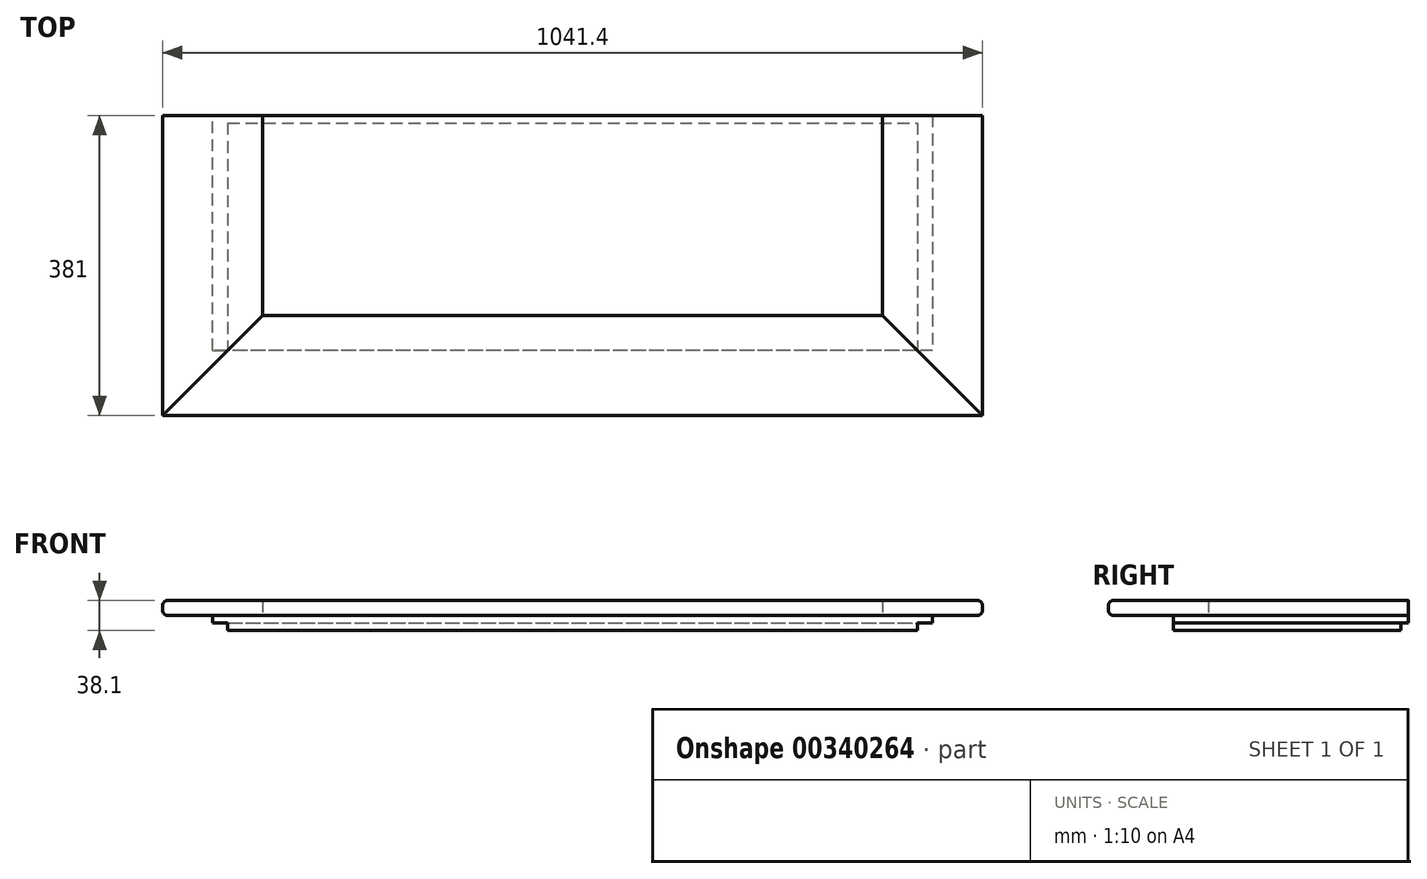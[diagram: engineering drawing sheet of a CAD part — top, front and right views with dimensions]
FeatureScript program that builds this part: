
annotation { "Feature Type Name" : "Feature", "Feature Type Description" : "" }
export const myFeature = defineFeature(function(context is Context, id is Id, definition is map)
    precondition{}
    {
        {
            var Q0;
            Q0=qCreatedBy(makeId("Top.planeOp"),FACE);
            var sketch = newSketch(context, id + "F0", { "sketchPlane" : qUnion([Q0])});
            skLineSegment(sketch, "E0.bottom", {"start": v(457.2, -149.22) * mm, "end": v(-457.2, -149.23) * mm});
            skLineSegment(sketch, "E0.top", {"start": v(457.2, 149.23) * mm, "end": v(-457.2, 149.22) * mm});
            skLineSegment(sketch, "E0.left", {"start": v(457.2, -149.22) * mm, "end": v(457.2, 149.23) * mm});
            skLineSegment(sketch, "E0.right", {"start": v(-457.2, -149.23) * mm, "end": v(-457.2, 149.22) * mm});
            skPoint(sketch, "E0.middle", {"position": v(0, 0) * mm});
            skSolve(sketch);
        }
        {
            var Q0;
            Q0 = qSketchRegion(id + "F0", true);
            extrude(context, id + "F1", {"entities" : qUnion([Q0]), "depth" : 19.05 * mm});
        }
        {
            var Q0;
            Q0=makeQuery(id+"F1.opExtrude","SWEPT_FACE",FACE,{"disambiguationData":[OSD([sQuery(id+"F0.wireOp",EDGE,"E0.left")])]});
            var sketch = newSketch(context, id + "F2", { "sketchPlane" : qUnion([Q0])});
            skLineSegment(sketch, "E1.bottom", {"start": v(149.23, 9.53) * mm, "end": v(139.7, 9.53) * mm});
            skLineSegment(sketch, "E1.top", {"start": v(149.23, 0) * mm, "end": v(139.7, 0) * mm});
            skLineSegment(sketch, "E1.left", {"start": v(149.23, 9.53) * mm, "end": v(149.23, 0) * mm});
            skLineSegment(sketch, "E1.right", {"start": v(139.7, 9.53) * mm, "end": v(139.7, 0) * mm});
            skSolve(sketch);
        }
        {
            var Q0;
            Q0 = qSketchRegion(id + "F2", true);
            extrude(context, id + "F3", {"entities" : qUnion([Q0]), "operationType" : NewBodyOperationType.REMOVE, "endBound" : BoundingType.THROUGH_ALL, "oppositeDirection" : true, "depth" : 25.4 * mm});
        }
        {
            var Q0;
            Q0=makeQuery(id+"F1.opExtrude","SWEPT_FACE",FACE,{"disambiguationData":[OSD([sQuery(id+"F0.wireOp",EDGE,"E0.bottom")])]});
            var sketch = newSketch(context, id + "F4", { "sketchPlane" : qUnion([Q0])});
            skLineSegment(sketch, "E2.bottom", {"start": v(-457.2, 9.53) * mm, "end": v(-438.15, 9.53) * mm});
            skLineSegment(sketch, "E2.top", {"start": v(-457.2, 0) * mm, "end": v(-438.15, 0) * mm});
            skLineSegment(sketch, "E2.left", {"start": v(-457.2, 9.53) * mm, "end": v(-457.2, 0) * mm});
            skLineSegment(sketch, "E2.right", {"start": v(-438.15, 9.53) * mm, "end": v(-438.15, 0) * mm});
            skLineSegment(sketch, "E3", {"start": v(0, 19.05) * mm, "end": v(0, 0) * mm, "construction": true});
            skLineSegment(sketch, "E4.MirrorCS", {"start": v(438.15, 9.52) * mm, "end": v(438.15, 0) * mm});
            skLineSegment(sketch, "E5.MirrorCS", {"start": v(457.2, 9.52) * mm, "end": v(457.2, 0) * mm});
            skLineSegment(sketch, "E6.MirrorCS", {"start": v(457.2, 0) * mm, "end": v(438.15, 0) * mm});
            skLineSegment(sketch, "E7.MirrorCS", {"start": v(457.2, 9.53) * mm, "end": v(438.15, 9.53) * mm});
            skSolve(sketch);
        }
        {
            var Q0;
            Q0 = qSketchRegion(id + "F4", true);
            extrude(context, id + "F5", {"entities" : qUnion([Q0]), "operationType" : NewBodyOperationType.REMOVE, "endBound" : BoundingType.THROUGH_ALL, "oppositeDirection" : true, "depth" : 25.4 * mm});
        }
        {
            var Q0;
            Q0=makeQuery(id+"F1.opExtrude","CAP_FACE",FACE,{"disambiguationData":[OSD([sQuery(id+"F0.wireOp",EDGE,"E0.bottom"),sQuery(id+"F0.wireOp",EDGE,"E0.top"),sQuery(id+"F0.wireOp",EDGE,"E0.left"),sQuery(id+"F0.wireOp",EDGE,"E0.right")])],"isStart":false});
            var sketch = newSketch(context, id + "F6", { "sketchPlane" : qUnion([Q0])});
            skLineSegment(sketch, "E8.bottom", {"start": v(-393.7, -104.78) * mm, "end": v(393.7, -104.77) * mm});
            skLineSegment(sketch, "E8.top", {"start": v(-520.7, -231.78) * mm, "end": v(520.7, -231.77) * mm});
            skLineSegment(sketch, "E9", {"start": v(-520.7, -231.78) * mm, "end": v(-393.7, -104.78) * mm});
            skLineSegment(sketch, "E10", {"start": v(520.7, -231.77) * mm, "end": v(393.7, -104.77) * mm});
            skSolve(sketch);
        }
        {
            var Q0;
            Q0 = qSketchRegion(id + "F6", true);
            extrude(context, id + "F7", {"entities" : qUnion([Q0]), "depth" : 19.05 * mm});
        }
        {
            var Q0;
            Q0=makeQuery(id+"F1.opExtrude","CAP_FACE",FACE,{"disambiguationData":[OSD([sQuery(id+"F0.wireOp",EDGE,"E0.bottom"),sQuery(id+"F0.wireOp",EDGE,"E0.top"),sQuery(id+"F0.wireOp",EDGE,"E0.left"),sQuery(id+"F0.wireOp",EDGE,"E0.right")])],"isStart":false});
            var sketch = newSketch(context, id + "F8", { "sketchPlane" : qUnion([Q0])});
            skLineSegment(sketch, "E11.bottom", {"start": v(-520.7, 149.22) * mm, "end": v(-393.7, 149.22) * mm});
            skLineSegment(sketch, "E11.left", {"start": v(-520.7, 149.22) * mm, "end": v(-520.7, -231.78) * mm});
            skLineSegment(sketch, "E11.right", {"start": v(-393.7, 149.22) * mm, "end": v(-393.7, -104.77) * mm});
            skLineSegment(sketch, "E12", {"start": v(-520.7, -231.78) * mm, "end": v(-393.7, -104.77) * mm});
            skSolve(sketch);
        }
        {
            var Q0;
            Q0 = qSketchRegion(id + "F8", true);
            extrude(context, id + "F9", {"entities" : qUnion([Q0]), "depth" : 19.05 * mm});
        }
        {
            var Q0;
            Q0=makeQuery(id+"F1.opExtrude","CAP_FACE",FACE,{"disambiguationData":[OSD([sQuery(id+"F0.wireOp",EDGE,"E0.bottom"),sQuery(id+"F0.wireOp",EDGE,"E0.top"),sQuery(id+"F0.wireOp",EDGE,"E0.left"),sQuery(id+"F0.wireOp",EDGE,"E0.right")])],"isStart":false});
            var sketch = newSketch(context, id + "F10", { "sketchPlane" : qUnion([Q0])});
            skLineSegment(sketch, "E13.bottom", {"start": v(393.7, 149.23) * mm, "end": v(520.7, 149.23) * mm});
            skLineSegment(sketch, "E13.left", {"start": v(393.7, 149.23) * mm, "end": v(393.7, -104.78) * mm});
            skLineSegment(sketch, "E13.right", {"start": v(520.7, 149.23) * mm, "end": v(520.7, -231.77) * mm});
            skLineSegment(sketch, "E14", {"start": v(520.7, -231.77) * mm, "end": v(393.7, -104.77) * mm});
            skSolve(sketch);
        }
        {
            var Q0;
            Q0 = qSketchRegion(id + "F10", true);
            extrude(context, id + "F11", {"entities" : qUnion([Q0]), "depth" : 19.05 * mm});
        }
        {
            var Q0;
            Q0=makeQuery(id+"F7.opExtrude","CAP_EDGE",EDGE,{"disambiguationData":[OSD([sQuery(id+"F6.wireOp",EDGE,"E8.top")])],"isStart":false});
            var Q1;
            Q1=makeQuery(id+"F7.opExtrude","CAP_EDGE",EDGE,{"disambiguationData":[OSD([sQuery(id+"F6.wireOp",EDGE,"E8.top")])],"isStart":true});
            var Q2;
            Q2=makeQuery(id+"F11.opExtrude","CAP_EDGE",EDGE,{"disambiguationData":[OSD([sQuery(id+"F10.wireOp",EDGE,"E13.right")])],"isStart":true});
            var Q3;
            Q3=makeQuery(id+"F11.opExtrude","CAP_EDGE",EDGE,{"disambiguationData":[OSD([sQuery(id+"F10.wireOp",EDGE,"E13.right")])],"isStart":false});
            var Q4;
            Q4=makeQuery(id+"F9.opExtrude","CAP_EDGE",EDGE,{"disambiguationData":[OSD([sQuery(id+"F8.wireOp",EDGE,"E11.left")])],"isStart":false});
            var Q5;
            Q5=makeQuery(id+"F9.opExtrude","CAP_EDGE",EDGE,{"disambiguationData":[OSD([sQuery(id+"F8.wireOp",EDGE,"E11.left")])],"isStart":true});
            fillet(context, id + "F12", {"entities" : qUnion([Q0, Q1, Q2, Q3, Q4, Q5]), "radius" : 6.35 * mm, "tangentPropagation" : true, "allowEdgeOverflow" : false});
        }
    });
